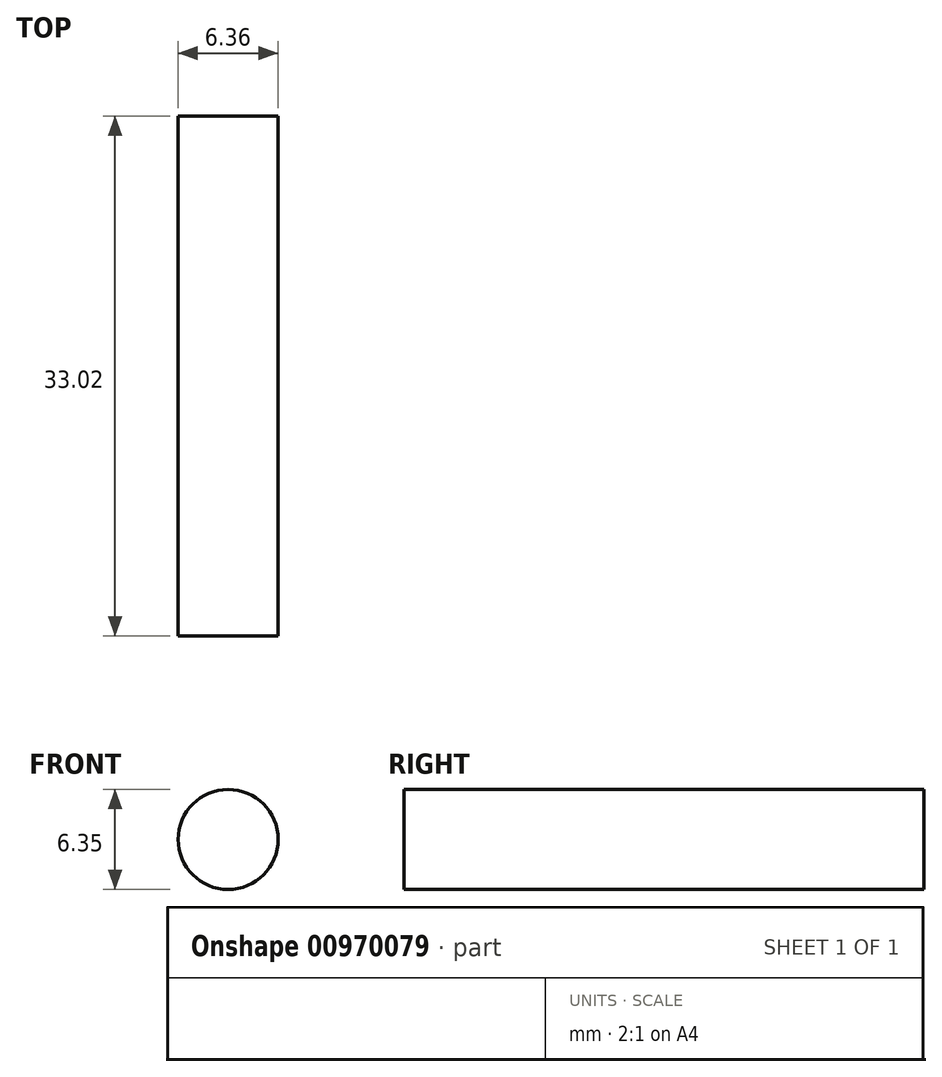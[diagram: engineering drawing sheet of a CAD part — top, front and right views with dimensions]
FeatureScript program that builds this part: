
annotation { "Feature Type Name" : "Feature", "Feature Type Description" : "" }
export const myFeature = defineFeature(function(context is Context, id is Id, definition is map)
    precondition{}
    {
        {
            var Q0;
            Q0=qCreatedBy(makeId("Right.planeOp"),FACE);
            var sketch = newSketch(context, id + "F0", { "sketchPlane" : qUnion([Q0])});
            skLineSegment(sketch, "E0.bottom", {"start": v(24.42, 18.63) * mm, "end": v(-8.6, 18.63) * mm});
            skLineSegment(sketch, "E0.top", {"start": v(24.42, 12.28) * mm, "end": v(-8.6, 12.28) * mm});
            skLineSegment(sketch, "E0.left", {"start": v(24.42, 18.63) * mm, "end": v(24.42, 12.28) * mm});
            skLineSegment(sketch, "E0.right", {"start": v(-8.6, 18.63) * mm, "end": v(-8.6, 12.28) * mm});
            skLineSegment(sketch, "E1", {"start": v(24.42, 15.45) * mm, "end": v(-8.6, 15.45) * mm});
            skSolve(sketch);
        }
        {
            var Q0;
            {var subQ0=sQuery(id+"F0.wireOp",EDGE,"E0.bottom");Q0=makeQuery(id+"F0.imprint","IMPRINT",FACE,{"disambiguationData":[TD([[makeQuery(id+"F0.imprint","IMPRINT",EDGE,{"derivedFrom":subQ0}),1.0]])]});}
            var Q1;
            Q1=sQuery(id+"F0.wireOp",EDGE,"E1");
            revolve(context, id + "F1", {"surfaceOperationType" : NewSurfaceOperationType.NEW, "entities" : qUnion([Q0]), "axis" : qUnion([Q1]), "revolveType" : RevolveType.FULL});
        }
    });
